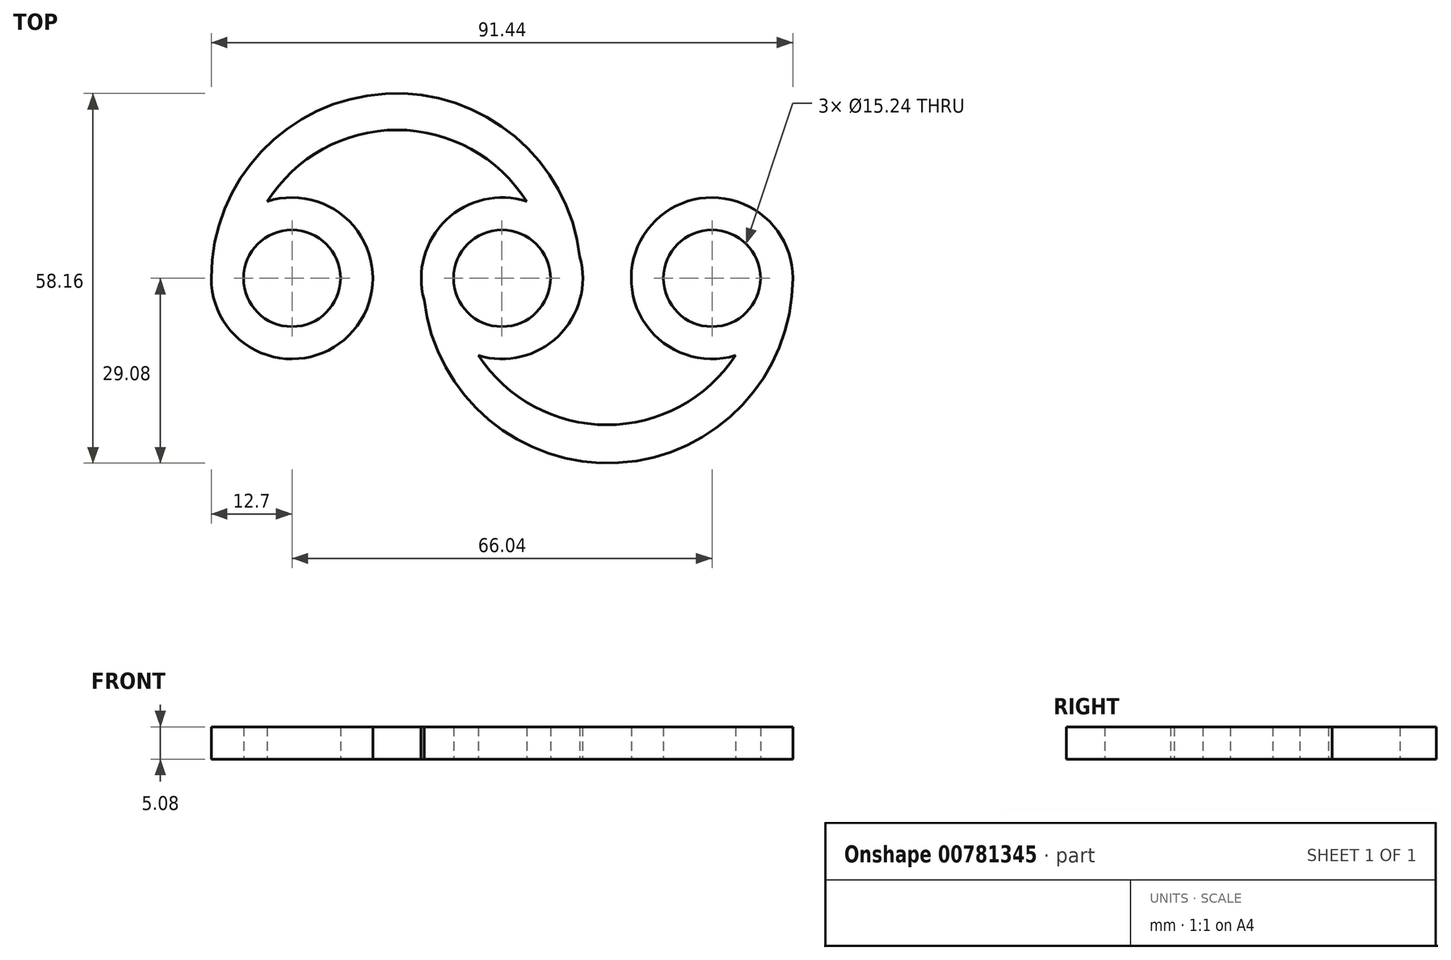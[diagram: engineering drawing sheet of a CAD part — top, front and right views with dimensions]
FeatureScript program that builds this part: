
annotation { "Feature Type Name" : "Feature", "Feature Type Description" : "" }
export const myFeature = defineFeature(function(context is Context, id is Id, definition is map)
    precondition{}
    {
        {
            var Q0;
            Q0=qCreatedBy(makeId("Top.planeOp"),FACE);
            var sketch = newSketch(context, id + "F0", { "sketchPlane" : qUnion([Q0])});
            skCircle(sketch, "E0", {"center": v(0, 0) * mm, "radius": 7.62 * mm});
            skCircle(sketch, "E1", {"center": v(-33.02, 0) * mm, "radius": 7.62 * mm});
            skCircle(sketch, "E2", {"center": v(33.02, 0) * mm, "radius": 7.62 * mm});
            skCircle(sketch, "E3", {"center": v(-33.02, 0) * mm, "radius": 12.7 * mm});
            skCircle(sketch, "E4", {"center": v(0, 0) * mm, "radius": 12.7 * mm});
            skCircle(sketch, "E5", {"center": v(33.02, 0) * mm, "radius": 12.7 * mm});
            skArc(sketch, "E6", {"start": v(12.44, 0) * mm, "mid": v(-16.64, 29.08) * mm, "end": v(-45.72, 0) * mm});
            skArc(sketch, "E7", {"start": v(-12.44, 0) * mm, "mid": v(16.64, -29.08) * mm, "end": v(45.72, 0) * mm});
            skArc(sketch, "E8", {"start": v(7.62, 0) * mm, "mid": v(-16.51, 23.33) * mm, "end": v(-40.64, 0) * mm});
            skArc(sketch, "E9", {"start": v(-7.62, 0) * mm, "mid": v(16.51, -23.07) * mm, "end": v(40.64, 0) * mm});
            skSolve(sketch);
        }
        {
            var Q0;
            {var subQ0=sQuery(id+"F0.wireOp",EDGE,"vTSgWgpr-l7dI-uBOk-7VNJ-Z3JP9AeVzrP9.right");Q0=makeQuery(id+"F0.imprint","IMPRINT",FACE,{"disambiguationData":[TD([[makeQuery(id+"F0.imprint","IMPRINT",EDGE,{"derivedFrom":subQ0}),-1.0]])]});}
            var Q1;
            {var subQ7=sQuery(id+"F0.wireOp",EDGE,"E8");var subQ9=sQuery(id+"F0.wireOp",EDGE,"E0");var subQ10=makeQuery(id+"F0.imprint","INTERSECT",VERTEX,{"disambiguationData":[OD(0.0)],"derivedFrom":[subQ9,subQ7]});Q1=makeQuery(id+"F0.imprint","IMPRINT",FACE,{"disambiguationData":[TD([[makeQuery(id+"F0.imprint","IMPRINT",EDGE,{"disambiguationData":[TD([[subQ10,-1.0]])],"derivedFrom":subQ9}),-1.0]])]});}
            var Q2;
            {var subQ0=sQuery(id+"F0.wireOp",EDGE,"E6");var subQ1=sQuery(id+"F0.wireOp",EDGE,"E3");var subQ2=makeQuery(id+"F0.imprint","INTERSECT",VERTEX,{"derivedFrom":[subQ1,subQ0]});Q2=makeQuery(id+"F0.imprint","IMPRINT",FACE,{"disambiguationData":[TD([[makeQuery(id+"F0.imprint","IMPRINT",EDGE,{"disambiguationData":[TD([[subQ2,1.0]])],"derivedFrom":subQ1}),-1.0]])]});}
            var Q3;
            {var subQ2=sQuery(id+"F0.wireOp",EDGE,"E8");var subQ4=sQuery(id+"F0.wireOp",EDGE,"E1");var subQ5=makeQuery(id+"F0.imprint","INTERSECT",VERTEX,{"disambiguationData":[OD(0.0)],"derivedFrom":[subQ4,subQ2]});Q3=makeQuery(id+"F0.imprint","IMPRINT",FACE,{"disambiguationData":[TD([[makeQuery(id+"F0.imprint","IMPRINT",EDGE,{"disambiguationData":[TD([[subQ5,1.0]])],"derivedFrom":subQ4}),-1.0]])]});}
            var Q4;
            {var subQ0=sQuery(id+"F0.wireOp",EDGE,"E7");var subQ1=sQuery(id+"F0.wireOp",EDGE,"E4");var subQ2=makeQuery(id+"F0.imprint","INTERSECT",VERTEX,{"derivedFrom":[subQ1,subQ0]});Q4=makeQuery(id+"F0.imprint","IMPRINT",FACE,{"disambiguationData":[TD([[makeQuery(id+"F0.imprint","IMPRINT",EDGE,{"disambiguationData":[TD([[subQ2,-1.0]])],"derivedFrom":subQ1}),-1.0]])]});}
            var Q5;
            {var subQ2=sQuery(id+"F0.wireOp",EDGE,"E9");var subQ5=sQuery(id+"F0.wireOp",EDGE,"E2");var subQ6=makeQuery(id+"F0.imprint","INTERSECT",VERTEX,{"disambiguationData":[OD(0.0)],"derivedFrom":[subQ5,subQ2]});Q5=makeQuery(id+"F0.imprint","IMPRINT",FACE,{"disambiguationData":[TD([[makeQuery(id+"F0.imprint","IMPRINT",EDGE,{"disambiguationData":[TD([[subQ6,-1.0]])],"derivedFrom":subQ5}),-1.0]])]});}
            var Q6;
            {var subQ0=sQuery(id+"F0.wireOp",EDGE,"vTSgWgpr-l7dI-uBOk-7VNJ-Z3JP9AeVzrP9.top");Q6=makeQuery(id+"F0.imprint","IMPRINT",FACE,{"disambiguationData":[TD([[makeQuery(id+"F0.imprint","IMPRINT",EDGE,{"derivedFrom":subQ0}),-1.0]])]});}
            var Q7;
            {var subQ0=sQuery(id+"F0.wireOp",EDGE,"BhER4y0l-lJNg-lcEi-G13w-GfGcIE4rgzST.bottom");Q7=makeQuery(id+"F0.imprint","IMPRINT",FACE,{"disambiguationData":[TD([[makeQuery(id+"F0.imprint","IMPRINT",EDGE,{"derivedFrom":subQ0}),-1.0]])]});}
            var Q8;
            {var subQ2=sQuery(id+"F0.wireOp",EDGE,"E9");var subQ4=sQuery(id+"F0.wireOp",EDGE,"E0");var subQ5=makeQuery(id+"F0.imprint","INTERSECT",VERTEX,{"disambiguationData":[OD(0.0)],"derivedFrom":[subQ4,subQ2]});Q8=makeQuery(id+"F0.imprint","IMPRINT",FACE,{"disambiguationData":[TD([[makeQuery(id+"F0.imprint","IMPRINT",EDGE,{"disambiguationData":[TD([[subQ5,1.0]])],"derivedFrom":subQ4}),-1.0]])]});}
            extrude(context, id + "F1", {"entities" : qUnion([Q0, Q1, Q2, Q3, Q4, Q5, Q6, Q7, Q8]), "depth" : 5.08 * mm, "offsetDistance" : 25.4 * mm});
        }
    });
